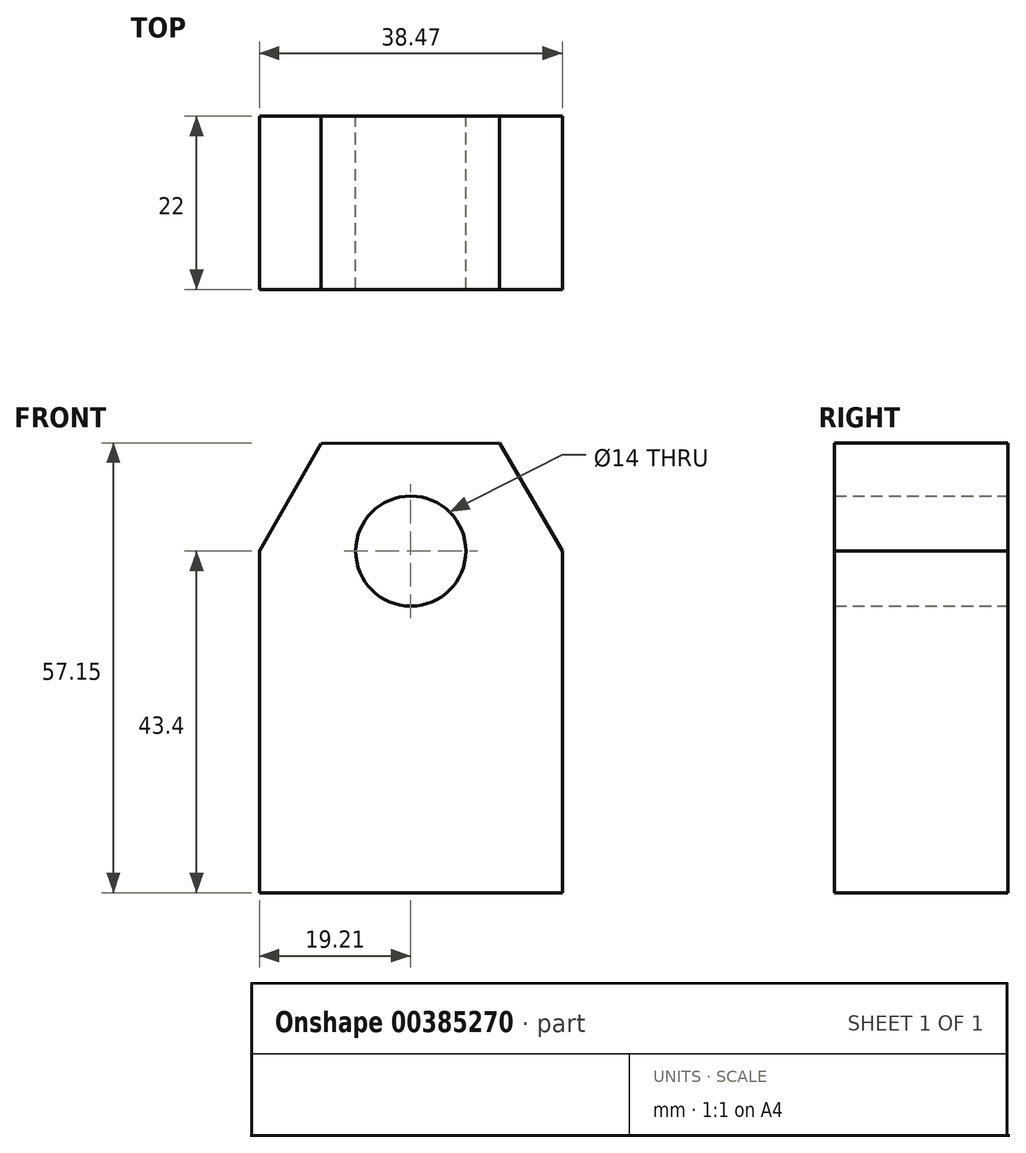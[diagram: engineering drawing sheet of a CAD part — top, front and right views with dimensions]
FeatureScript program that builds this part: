
annotation { "Feature Type Name" : "Feature", "Feature Type Description" : "" }
export const myFeature = defineFeature(function(context is Context, id is Id, definition is map)
    precondition{}
    {
        {
            var Q0;
            Q0=qCreatedBy(makeId("Front.planeOp"),FACE);
            var sketch = newSketch(context, id + "F0", { "sketchPlane" : qUnion([Q0])});
            skCircle(sketch, "E0", {"center": v(0, 0) * mm, "radius": 7 * mm});
            skLineSegment(sketch, "E1", {"start": v(-19.21, 0) * mm, "end": v(-19.21, -43.4) * mm});
            skLineSegment(sketch, "E2", {"start": v(19.26, -43.4) * mm, "end": v(-19.21, -43.4) * mm});
            skLineSegment(sketch, "E3.0", {"start": v(11.24, 13.75) * mm, "end": v(19.26, 0) * mm});
            skLineSegment(sketch, "E3.4", {"start": v(-19.21, 0) * mm, "end": v(-11.41, 13.65) * mm});
            skLineSegment(sketch, "E3.5", {"start": v(-11.41, 13.65) * mm, "end": v(11.24, 13.75) * mm});
            skLineSegment(sketch, "E4", {"start": v(19.26, 0) * mm, "end": v(19.26, -43.4) * mm});
            skSolve(sketch);
        }
        {
            var Q0;
            Q0=makeQuery(id+"F0.imprint","IMPRINT",FACE,{"disambiguationData":[TD([[makeQuery(id+"F0.imprint","IMPRINT",EDGE,{"derivedFrom":sQuery(id+"F0.wireOp",EDGE,"E0")}),-1.0]])]});
            extrude(context, id + "F1", {"entities" : qUnion([Q0]), "depth" : 22 * mm});
        }
    });
